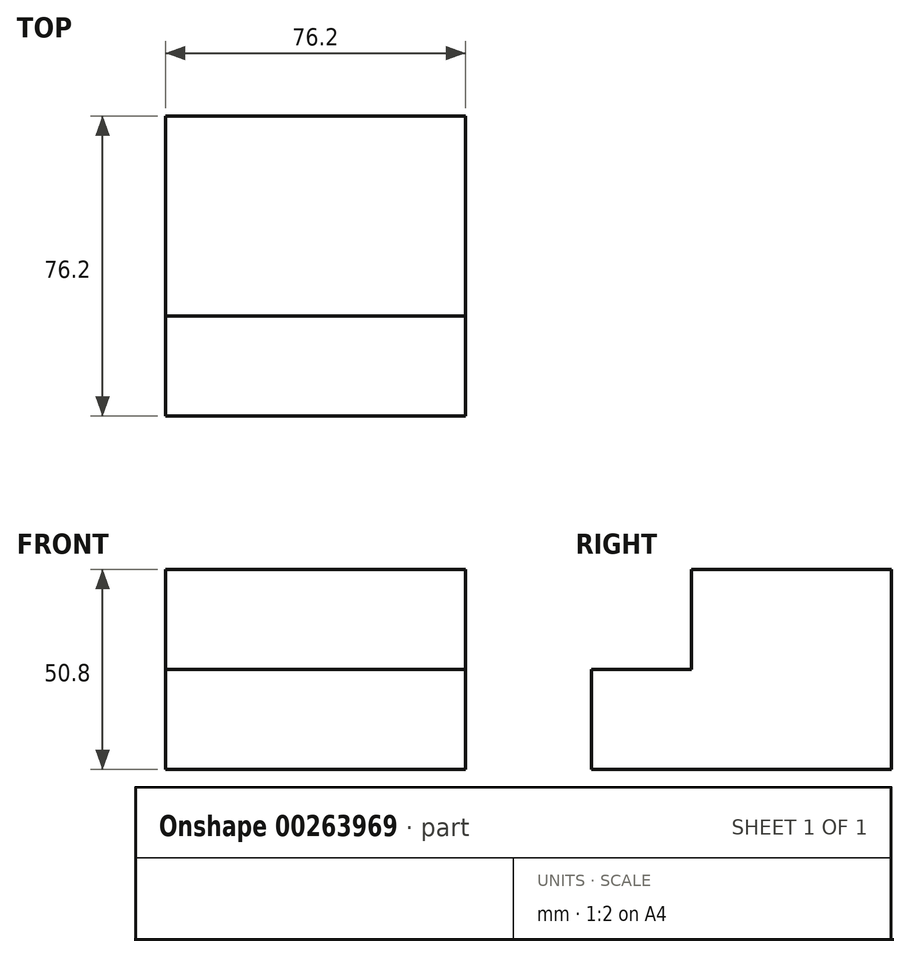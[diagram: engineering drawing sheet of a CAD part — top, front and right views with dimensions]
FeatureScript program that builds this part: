
annotation { "Feature Type Name" : "Feature", "Feature Type Description" : "" }
export const myFeature = defineFeature(function(context is Context, id is Id, definition is map)
    precondition{}
    {
        {
            var Q0;
            Q0=qCreatedBy(makeId("Right.planeOp"),FACE);
            var sketch = newSketch(context, id + "F0", { "sketchPlane" : qUnion([Q0])});
            skLineSegment(sketch, "E0", {"start": v(-41.46, -76.24) * mm, "end": v(34.74, -76.24) * mm});
            skLineSegment(sketch, "E1", {"start": v(34.74, -76.24) * mm, "end": v(34.74, -25.44) * mm});
            skLineSegment(sketch, "E2", {"start": v(34.74, -25.44) * mm, "end": v(-16.06, -25.44) * mm});
            skLineSegment(sketch, "E3", {"start": v(-16.06, -25.44) * mm, "end": v(-16.06, -50.84) * mm});
            skLineSegment(sketch, "E4", {"start": v(-16.06, -50.84) * mm, "end": v(-41.46, -50.84) * mm});
            skLineSegment(sketch, "E5", {"start": v(-41.46, -50.84) * mm, "end": v(-41.46, -76.24) * mm});
            skSolve(sketch);
        }
        {
            var Q0;
            Q0=makeQuery(id+"F0.imprint","IMPRINT",FACE,{"disambiguationData":[TD([[makeQuery(id+"F0.imprint","IMPRINT",EDGE,{"derivedFrom":sQuery(id+"F0.wireOp",EDGE,"E0")}),1.0]])]});
            extrude(context, id + "F1", {"entities" : qUnion([Q0]), "oppositeDirection" : true, "depth" : 76.2 * mm});
        }
    });
